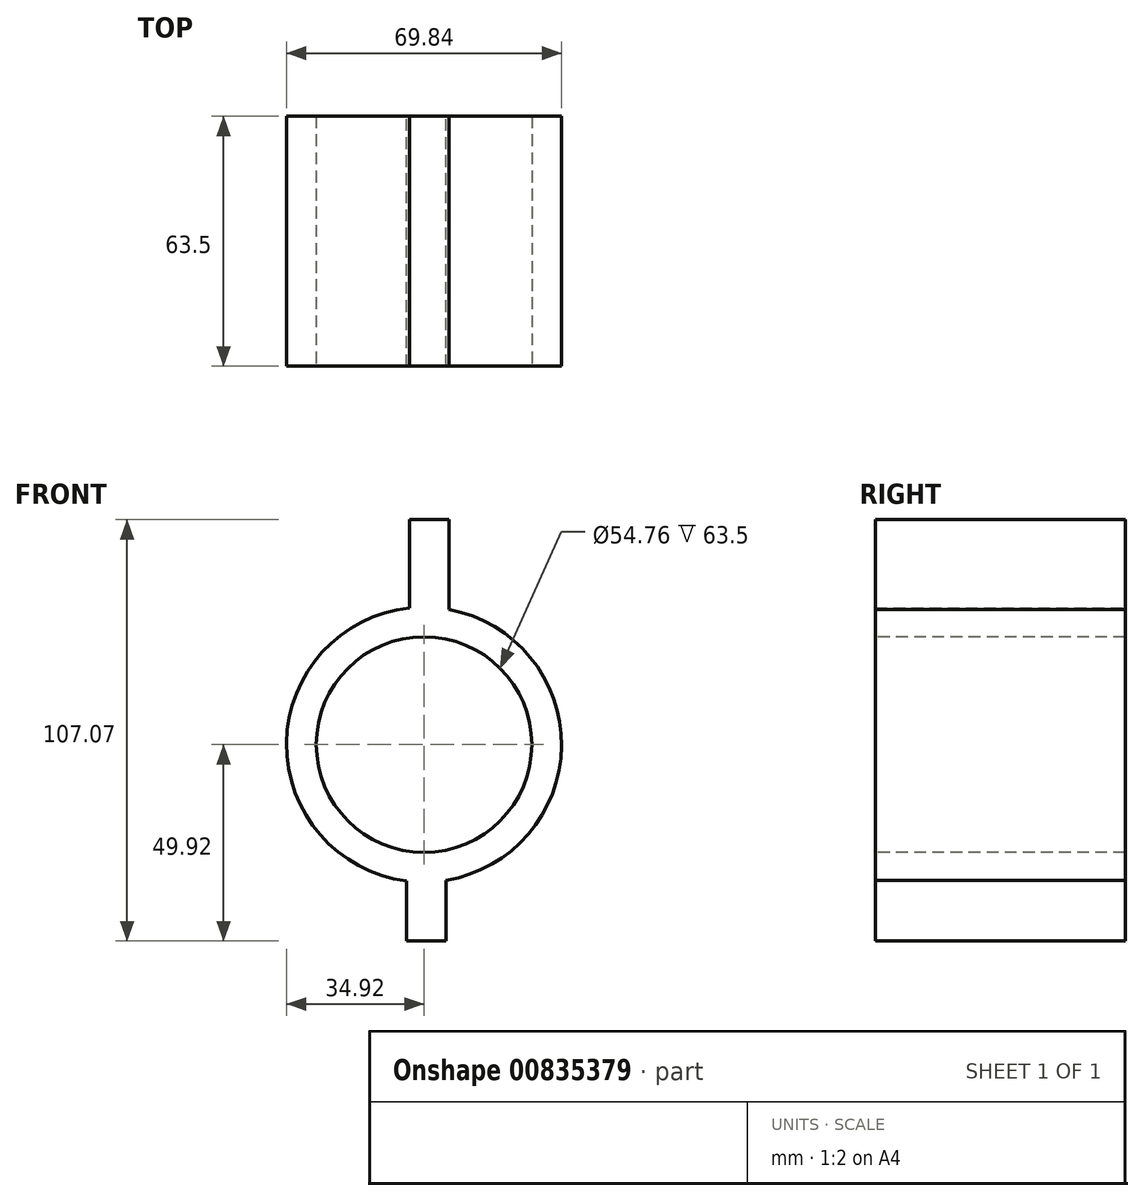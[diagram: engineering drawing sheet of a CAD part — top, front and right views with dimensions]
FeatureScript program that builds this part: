
annotation { "Feature Type Name" : "Feature", "Feature Type Description" : "" }
export const myFeature = defineFeature(function(context is Context, id is Id, definition is map)
    precondition{}
    {
        {
            var Q0;
            Q0=qCreatedBy(makeId("Front.planeOp"),FACE);
            var sketch = newSketch(context, id + "F0", { "sketchPlane" : qUnion([Q0])});
            skCircle(sketch, "E0", {"center": v(0, 0) * mm, "radius": 34.93 * mm});
            skLineSegment(sketch, "E1.top", {"start": v(6.38, 57.15) * mm, "end": v(-3.7, 57.15) * mm});
            skLineSegment(sketch, "E1.left", {"start": v(6.38, 34.34) * mm, "end": v(6.38, 57.15) * mm});
            skLineSegment(sketch, "E1.right", {"start": v(-3.7, 34.34) * mm, "end": v(-3.7, 57.15) * mm});
            skLineSegment(sketch, "E2.bottom", {"start": v(5.64, -49.92) * mm, "end": v(-4.45, -49.92) * mm});
            skLineSegment(sketch, "E2.left", {"start": v(5.64, -49.92) * mm, "end": v(5.64, -27.1) * mm});
            skLineSegment(sketch, "E2.right", {"start": v(-4.45, -49.92) * mm, "end": v(-4.45, -27.1) * mm});
            skSolve(sketch);
        }
        {
            var Q0;
            {var subQ4=sQuery(id+"F0.wireOp",EDGE,"E1.top");Q0=makeQuery(id+"F0.imprint","IMPRINT",FACE,{"disambiguationData":[TD([[makeQuery(id+"F0.imprint","IMPRINT",EDGE,{"derivedFrom":subQ4}),1.0]])]});}
            var Q1;
            {var subQ1=sQuery(id+"F0.wireOp",EDGE,"E1.bottom");Q1=makeQuery(id+"F0.imprint","IMPRINT",FACE,{"disambiguationData":[TD([[makeQuery(id+"F0.imprint","IMPRINT",EDGE,{"derivedFrom":subQ1}),1.0]])]});}
            var Q2;
            {var subQ4=sQuery(id+"F0.wireOp",EDGE,"E2.bottom");Q2=makeQuery(id+"F0.imprint","IMPRINT",FACE,{"disambiguationData":[TD([[makeQuery(id+"F0.imprint","IMPRINT",EDGE,{"derivedFrom":subQ4}),-1.0]])]});}
            var Q3;
            {var subQ0=sQuery(id+"F0.wireOp",EDGE,"E0");var subQ1=makeQuery(id+"F0.imprint","INTERSECT",VERTEX,{"derivedFrom":[subQ0,sQuery(id+"F0.wireOp",EDGE,"E1.left")]});Q3=makeQuery(id+"F0.imprint","IMPRINT",FACE,{"disambiguationData":[TD([[makeQuery(id+"F0.imprint","IMPRINT",EDGE,{"disambiguationData":[TD([[subQ1,-1.0]])],"derivedFrom":subQ0}),1.0]])]});}
            extrude(context, id + "F1", {"entities" : qUnion([Q0, Q1, Q2, Q3]), "depth" : 63.5 * mm, "offsetDistance" : 25.4 * mm});
        }
        {
            var Q0;
            Q0=makeQuery(id+"F1.opExtrude","CAP_FACE",FACE,{"disambiguationData":[OSD([sQuery(id+"F0.wireOp",EDGE,"E0"),sQuery(id+"F0.wireOp",EDGE,"E1.bottom"),sQuery(id+"F0.wireOp",EDGE,"E1.right"),sQuery(id+"F0.wireOp",EDGE,"E2.top"),sQuery(id+"F0.wireOp",EDGE,"E2.right")])],"isStart":false});
            var sketch = newSketch(context, id + "F2", { "sketchPlane" : qUnion([Q0])});
            skCircle(sketch, "E3", {"center": v(0, 0) * mm, "radius": 27.38 * mm});
            skSolve(sketch);
        }
        {
            var Q0;
            Q0=makeQuery(id+"F2.imprint","IMPRINT",FACE,{"disambiguationData":[TD([[makeQuery(id+"F2.imprint","IMPRINT",EDGE,{"derivedFrom":sQuery(id+"F2.wireOp",EDGE,"E3")}),1.0]])]});
            extrude(context, id + "F3", {"entities" : qUnion([Q0]), "operationType" : NewBodyOperationType.REMOVE, "oppositeDirection" : true, "depth" : 101.6 * mm, "offsetDistance" : 25.4 * mm});
        }
    });
